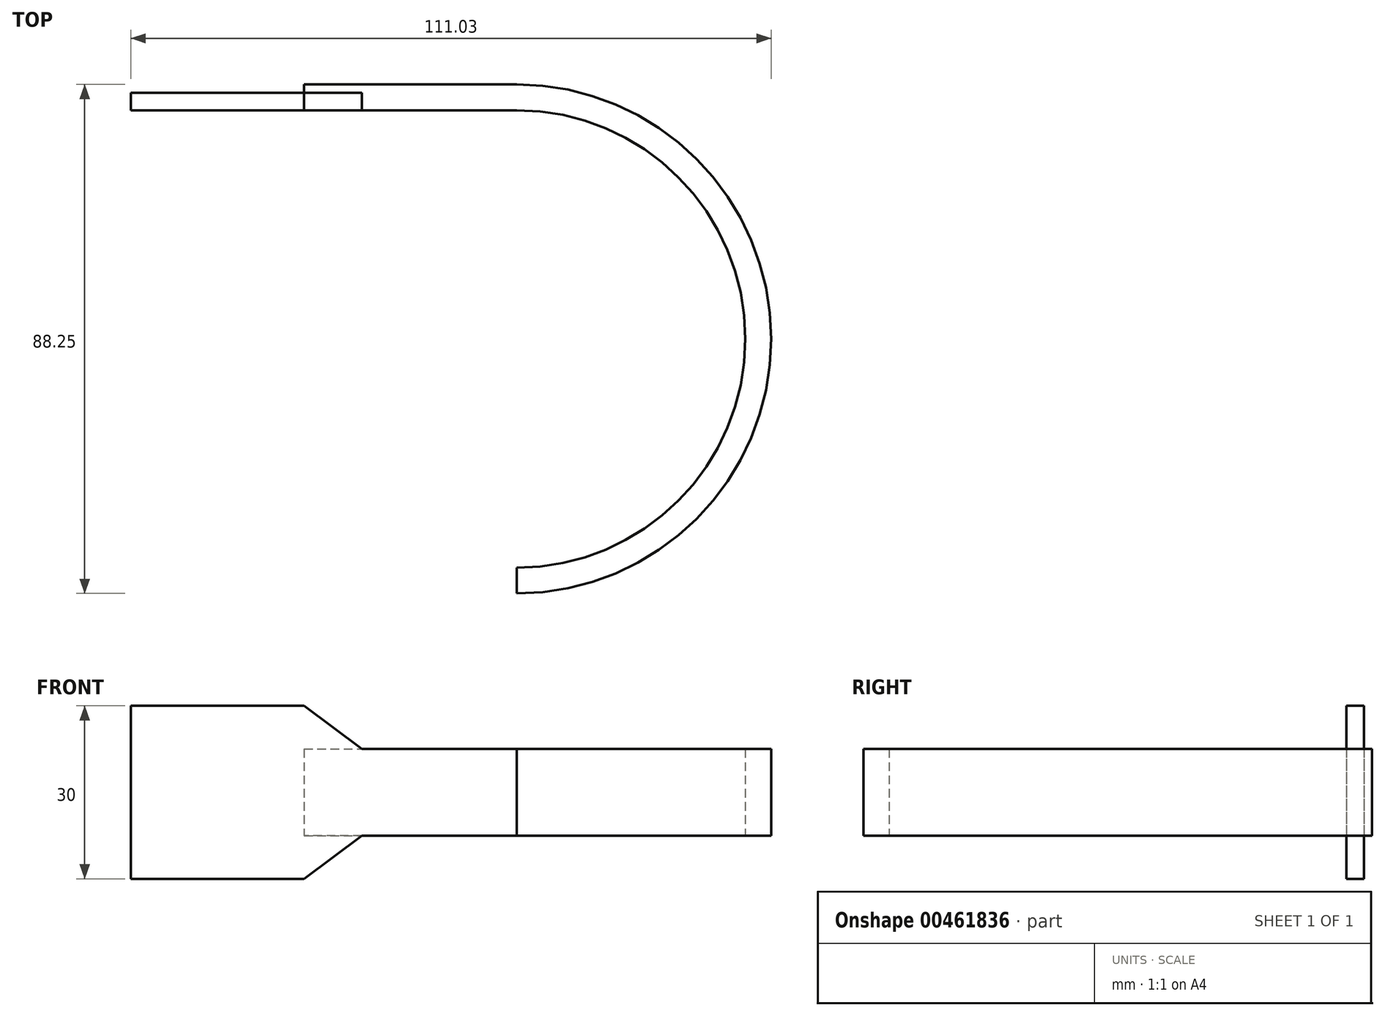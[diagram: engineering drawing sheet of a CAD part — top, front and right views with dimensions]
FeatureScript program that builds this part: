
annotation { "Feature Type Name" : "Feature", "Feature Type Description" : "" }
export const myFeature = defineFeature(function(context is Context, id is Id, definition is map)
    precondition{}
    {
        {
            var Q0;
            Q0=qCreatedBy(makeId("Top.planeOp"),FACE);
            var sketch = newSketch(context, id + "F0", { "sketchPlane" : qUnion([Q0])});
            skLineSegment(sketch, "E0", {"start": v(-20.01, 27.06) * mm, "end": v(46.9, 27.06) * mm});
            skLineSegment(sketch, "E1", {"start": v(46.9, 27.06) * mm, "end": v(46.9, 24.03) * mm});
            skLineSegment(sketch, "E2", {"start": v(46.9, 24.03) * mm, "end": v(-20.01, 24.03) * mm});
            skLineSegment(sketch, "E3", {"start": v(-20.01, 24.03) * mm, "end": v(-20.01, 27.06) * mm});
            skArc(sketch, "E4", {"start": v(46.9, -58.32) * mm, "mid": v(89.59, -15.63) * mm, "end": v(46.9, 27.06) * mm});
            skArc(sketch, "E5", {"start": v(46.9, -55.29) * mm, "mid": v(86.56, -15.63) * mm, "end": v(46.9, 24.03) * mm});
            skLineSegment(sketch, "E6", {"start": v(46.9, -55.29) * mm, "end": v(46.9, -58.32) * mm});
            skLineSegment(sketch, "E7", {"start": v(-20.01, 27.06) * mm, "end": v(10.02, 27.06) * mm});
            skLineSegment(sketch, "E8", {"start": v(10.02, 27.06) * mm, "end": v(10.02, 28.5) * mm});
            skLineSegment(sketch, "E9", {"start": v(10.02, 28.5) * mm, "end": v(46.9, 28.5) * mm});
            skLineSegment(sketch, "E10", {"start": v(46.9, 28.5) * mm, "end": v(46.9, 27.06) * mm});
            skArc(sketch, "E11", {"start": v(46.9, -59.75) * mm, "mid": v(91.02, -15.63) * mm, "end": v(46.9, 28.5) * mm});
            skLineSegment(sketch, "E12", {"start": v(46.9, -58.32) * mm, "end": v(46.9, -59.75) * mm});
            skPoint(sketch, "E13", {"position": v(10.02, 24.03) * mm});
            skLineSegment(sketch, "E14", {"start": v(10.02, 24.03) * mm, "end": v(10.02, 27.06) * mm});
            skSolve(sketch);
        }
        {
            var Q0;
            {var subQ0=sQuery(id+"F0.wireOp",EDGE,"E3");Q0=makeQuery(id+"F0.imprint","IMPRINT",FACE,{"disambiguationData":[TD([[makeQuery(id+"F0.imprint","IMPRINT",EDGE,{"derivedFrom":subQ0}),-1.0]])]});}
            extrude(context, id + "F1", {"entities" : qUnion([Q0]), "endBound" : BoundingType.SYMMETRIC, "depth" : 30 * mm});
        }
        {
            var Q0;
            Q0 = qSketchRegion(id + "F0", true);
            extrude(context, id + "F2", {"entities" : qUnion([Q0]), "operationType" : NewBodyOperationType.ADD, "endBound" : BoundingType.SYMMETRIC, "depth" : 15 * mm});
        }
        {
            var Q0;
            Q0=makeQuery(id+"F2.boolean.opBoolean","INTERSECT",EDGE,{"derivedFrom":[makeQuery(id+"F1.opExtrude","SWEPT_FACE",FACE,{"disambiguationData":[OSD([sQuery(id+"F0.wireOp",EDGE,"E14")])]}),makeQuery(id+"F2.opExtrude","CAP_FACE",FACE,{"disambiguationData":[OSD([sQuery(id+"F0.wireOp",EDGE,"E2"),sQuery(id+"F0.wireOp",EDGE,"E3"),sQuery(id+"F0.wireOp",EDGE,"E5"),sQuery(id+"F0.wireOp",EDGE,"E6"),sQuery(id+"F0.wireOp",EDGE,"E7"),sQuery(id+"F0.wireOp",EDGE,"E8"),sQuery(id+"F0.wireOp",EDGE,"E9"),sQuery(id+"F0.wireOp",EDGE,"E11"),sQuery(id+"F0.wireOp",EDGE,"E12")])],"isStart":false})]});
            chamfer(context, id + "F3", {"entities" : qUnion([Q0]), "chamferType" : ChamferType.TWO_OFFSETS, "width1" : 7.5 * mm, "oppositeDirection" : false, "width2" : 10 * mm, "tangentPropagation" : true});
        }
        {
            var Q0;
            Q0=makeQuery(id+"F2.boolean.opBoolean","INTERSECT",EDGE,{"derivedFrom":[makeQuery(id+"F1.opExtrude","SWEPT_FACE",FACE,{"disambiguationData":[OSD([sQuery(id+"F0.wireOp",EDGE,"E14")])]}),makeQuery(id+"F2.opExtrude","CAP_FACE",FACE,{"disambiguationData":[OSD([sQuery(id+"F0.wireOp",EDGE,"E2"),sQuery(id+"F0.wireOp",EDGE,"E3"),sQuery(id+"F0.wireOp",EDGE,"E5"),sQuery(id+"F0.wireOp",EDGE,"E6"),sQuery(id+"F0.wireOp",EDGE,"E7"),sQuery(id+"F0.wireOp",EDGE,"E8"),sQuery(id+"F0.wireOp",EDGE,"E9"),sQuery(id+"F0.wireOp",EDGE,"E11"),sQuery(id+"F0.wireOp",EDGE,"E12")])],"isStart":true})]});
            chamfer(context, id + "F4", {"entities" : qUnion([Q0]), "chamferType" : ChamferType.TWO_OFFSETS, "width1" : 10 * mm, "oppositeDirection" : false, "width2" : 7.5 * mm, "tangentPropagation" : true});
        }
    });
